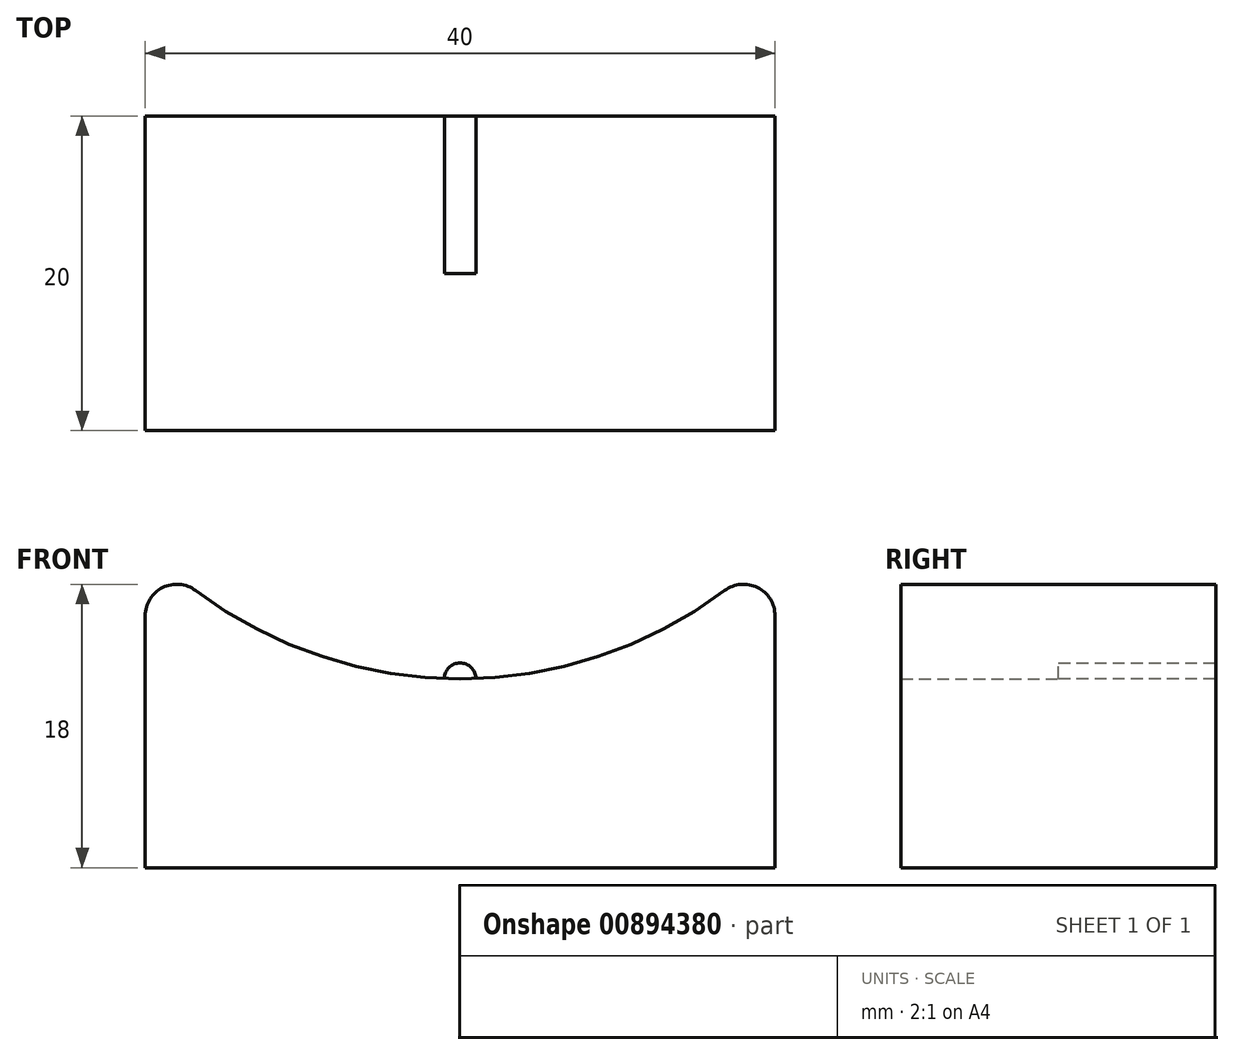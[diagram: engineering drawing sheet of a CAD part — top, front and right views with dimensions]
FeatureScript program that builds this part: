
annotation { "Feature Type Name" : "Feature", "Feature Type Description" : "" }
export const myFeature = defineFeature(function(context is Context, id is Id, definition is map)
    precondition{}
    {
        {
            var Q0;
            Q0=qCreatedBy(makeId("Front.planeOp"),FACE);
            var sketch = newSketch(context, id + "F0", { "sketchPlane" : qUnion([Q0])});
            skArc(sketch, "E0", {"start": v(20, -15) * mm, "mid": v(0, 25) * mm, "end": v(-20, -15) * mm, "construction": true});
            skArc(sketch, "E1.0", {"start": v(-16.8, -22.4) * mm, "mid": v(0, -28) * mm, "end": v(16.8, -22.4) * mm});
            skLineSegment(sketch, "E2.bottom", {"start": v(-20, -9.08) * mm, "end": v(20, -9.08) * mm, "construction": true});
            skLineSegment(sketch, "E2.top", {"start": v(-20, -40) * mm, "end": v(20, -40) * mm});
            skLineSegment(sketch, "E2.left", {"start": v(-20, -9.08) * mm, "end": v(-20, -15) * mm, "construction": true});
            skLineSegment(sketch, "E2.right", {"start": v(20, -9.08) * mm, "end": v(20, -15) * mm, "construction": true});
            skLineSegment(sketch, "E3.trimOffspring", {"start": v(20, -24) * mm, "end": v(20, -40) * mm});
            skLineSegment(sketch, "E4.trimOffspring", {"start": v(-20, -24) * mm, "end": v(-20, -40) * mm});
            skPoint(sketch, "E5.visualSharp", {"position": v(-20, -19.6) * mm});
            skArc(sketch, "E5.filletArc", {"start": v(-16.8, -22.4) * mm, "mid": v(-18.9, -22.21) * mm, "end": v(-20, -24) * mm});
            skPoint(sketch, "E6.visualSharp", {"position": v(20, -19.6) * mm});
            skArc(sketch, "E6.filletArc", {"start": v(20, -24) * mm, "mid": v(18.9, -22.21) * mm, "end": v(16.8, -22.4) * mm});
            skCircle(sketch, "E7", {"center": v(0, -28) * mm, "radius": 1 * mm});
            skSolve(sketch);
        }
        {
            var Q0;
            Q0=makeQuery(id+"F0.imprint","IMPRINT",FACE,{"disambiguationData":[TD([[makeQuery(id+"F0.imprint","IMPRINT",EDGE,{"derivedFrom":sQuery(id+"F0.wireOp",EDGE,"E2.top")}),1.0]])]});
            var Q1;
            {var subQ0=sQuery(id+"F0.wireOp",EDGE,"E7");var subQ1=sQuery(id+"F0.wireOp",EDGE,"E1.0");var subQ2=makeQuery(id+"F0.imprint","INTERSECT",VERTEX,{"disambiguationData":[OD(0.0)],"derivedFrom":[subQ1,subQ0]});Q1=makeQuery(id+"F0.imprint","IMPRINT",FACE,{"disambiguationData":[TD([[makeQuery(id+"F0.imprint","IMPRINT",EDGE,{"disambiguationData":[TD([[subQ2,-1.0]])],"derivedFrom":subQ1}),-1.0]])]});}
            extrude(context, id + "F1", {"entities" : qUnion([Q0, Q1]), "depth" : 20 * mm, "offsetDistance" : 25 * mm});
        }
        {
            var Q0;
            Q0 = qSketchRegion(id + "F0", true);
            extrude(context, id + "F2", {"entities" : qUnion([Q0]), "operationType" : NewBodyOperationType.ADD, "depth" : 10 * mm, "offsetDistance" : 25 * mm});
        }
    });
